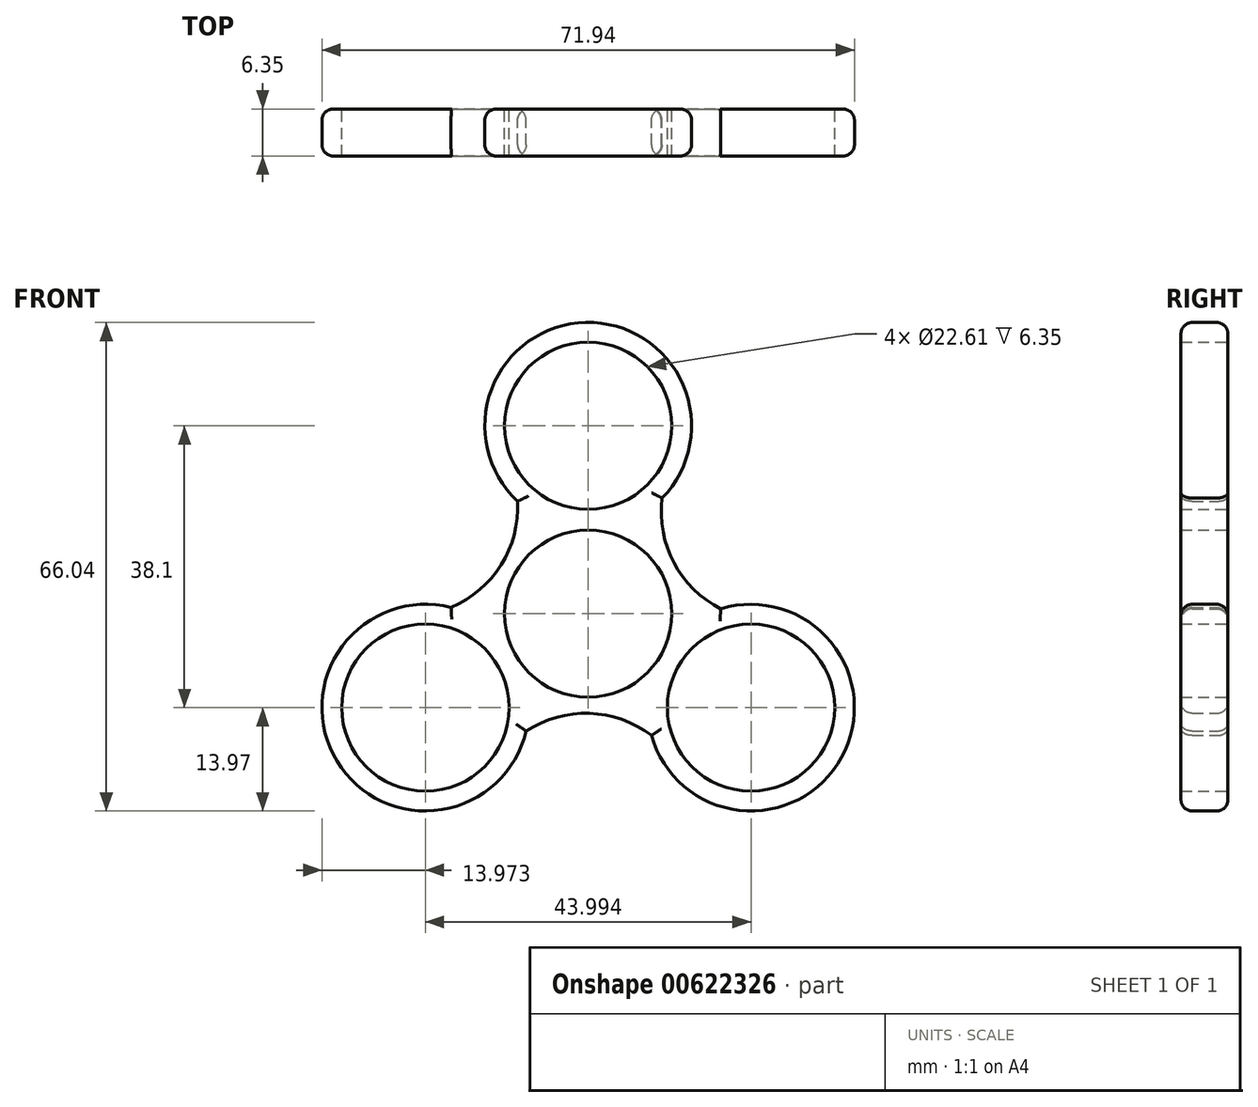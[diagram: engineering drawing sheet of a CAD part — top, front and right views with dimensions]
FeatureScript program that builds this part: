
annotation { "Feature Type Name" : "Feature", "Feature Type Description" : "" }
export const myFeature = defineFeature(function(context is Context, id is Id, definition is map)
    precondition{}
    {
        {
            var Q0;
            Q0=qCreatedBy(makeId("Front.planeOp"),FACE);
            var sketch = newSketch(context, id + "F0", { "sketchPlane" : qUnion([Q0])});
            skCircle(sketch, "E0", {"center": v(0, 0) * mm, "radius": 11.3 * mm});
            skCircle(sketch, "E1", {"center": v(0, 25.4) * mm, "radius": 11.3 * mm});
            skCircle(sketch, "E2.1.0", {"center": v(-22, -12.7) * mm, "radius": 11.3 * mm});
            skCircle(sketch, "E2.2.0", {"center": v(22, -12.7) * mm, "radius": 11.3 * mm});
            skArc(sketch, "E3", {"start": v(9.99, 15.63) * mm, "mid": v(-0.31, 39.37) * mm, "end": v(-9.54, 15.2) * mm});
            skArc(sketch, "E4.1.0", {"start": v(-18.53, 0.83) * mm, "mid": v(-33.94, -19.95) * mm, "end": v(-8.39, -15.86) * mm});
            skArc(sketch, "E4.2.0", {"start": v(8.54, -16.46) * mm, "mid": v(34.25, -19.41) * mm, "end": v(17.93, 0.66) * mm});
            skArc(sketch, "E5", {"start": v(9.99, 15.63) * mm, "mid": v(11.59, 6.9) * mm, "end": v(17.93, 0.66) * mm});
            skArc(sketch, "E6.1.0", {"start": v(-18.53, 0.83) * mm, "mid": v(-11.76, 6.6) * mm, "end": v(-9.54, 15.2) * mm});
            skArc(sketch, "E6.2.0", {"start": v(8.54, -16.46) * mm, "mid": v(0.17, -13.48) * mm, "end": v(-8.39, -15.86) * mm});
            skSolve(sketch);
        }
        {
            var Q0;
            Q0 = qSketchRegion(id + "F0", true);
            extrude(context, id + "F1", {"entities" : qUnion([Q0]), "depth" : 6.35 * mm, "offsetDistance" : 25.4 * mm});
        }
        {
            var Q0;
            Q0=makeQuery(id+"F1.opExtrude","CAP_EDGE",EDGE,{"disambiguationData":[OSD([sQuery(id+"F0.wireOp",EDGE,"E4.2.0")])],"isStart":false});
            var Q1;
            Q1=makeQuery(id+"F1.opExtrude","CAP_EDGE",EDGE,{"disambiguationData":[OSD([sQuery(id+"F0.wireOp",EDGE,"E6.2.0")])],"isStart":false});
            var Q2;
            Q2=makeQuery(id+"F1.opExtrude","CAP_EDGE",EDGE,{"disambiguationData":[OSD([sQuery(id+"F0.wireOp",EDGE,"E4.1.0")])],"isStart":false});
            var Q3;
            Q3=makeQuery(id+"F1.opExtrude","CAP_EDGE",EDGE,{"disambiguationData":[OSD([sQuery(id+"F0.wireOp",EDGE,"E6.1.0")])],"isStart":false});
            var Q4;
            Q4=makeQuery(id+"F1.opExtrude","CAP_EDGE",EDGE,{"disambiguationData":[OSD([sQuery(id+"F0.wireOp",EDGE,"E3")])],"isStart":false});
            var Q5;
            Q5=makeQuery(id+"F1.opExtrude","CAP_EDGE",EDGE,{"disambiguationData":[OSD([sQuery(id+"F0.wireOp",EDGE,"E5")])],"isStart":false});
            var Q6;
            Q6=makeQuery(id+"F1.opExtrude","CAP_EDGE",EDGE,{"disambiguationData":[OSD([sQuery(id+"F0.wireOp",EDGE,"E5")])],"isStart":true});
            var Q7;
            Q7=makeQuery(id+"F1.opExtrude","CAP_EDGE",EDGE,{"disambiguationData":[OSD([sQuery(id+"F0.wireOp",EDGE,"E4.2.0")])],"isStart":true});
            var Q8;
            Q8=makeQuery(id+"F1.opExtrude","CAP_EDGE",EDGE,{"disambiguationData":[OSD([sQuery(id+"F0.wireOp",EDGE,"E6.2.0")])],"isStart":true});
            var Q9;
            Q9=makeQuery(id+"F1.opExtrude","CAP_EDGE",EDGE,{"disambiguationData":[OSD([sQuery(id+"F0.wireOp",EDGE,"E4.1.0")])],"isStart":true});
            var Q10;
            Q10=makeQuery(id+"F1.opExtrude","CAP_EDGE",EDGE,{"disambiguationData":[OSD([sQuery(id+"F0.wireOp",EDGE,"E6.1.0")])],"isStart":true});
            var Q11;
            Q11=makeQuery(id+"F1.opExtrude","CAP_EDGE",EDGE,{"disambiguationData":[OSD([sQuery(id+"F0.wireOp",EDGE,"E3")])],"isStart":true});
            fillet(context, id + "F2", {"entities" : qUnion([Q0, Q1, Q2, Q3, Q4, Q5, Q6, Q7, Q8, Q9, Q10, Q11]), "radius" : 1.52 * mm, "tangentPropagation" : true, "allowEdgeOverflow" : false});
        }
    });
